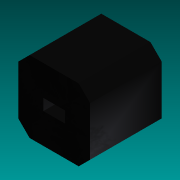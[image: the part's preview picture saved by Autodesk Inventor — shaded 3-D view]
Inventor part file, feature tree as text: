
AUTODESK INVENTOR PART (.ipt)
format: ipt  version: 2015 (Build 190159000, 159)  size: 91,648 bytes
history: native  units: mm
features: extrude x1, sketch x1
ambient origin geometry x8: Origin, YZ Plane, XZ Plane, XY Plane, X Axis, Y Axis, Z Axis, Center Point
bodies: Solid1 (feature_tree)
feature tree (2):
  extrude  "Extrusion1"  Depth=2.54mm
  sketch  "Sketch1"  dims[d0=2.54mm d1=2.54mm d2=0.406mm d3=0.762mm d4=0.4mm d5=0.4mm d6=0.4mm d7=0.4mm d8=0.4mm d9=0.4mm d10=0.4mm d11=0.4mm d12=2.54mm d13=0.0mm]
